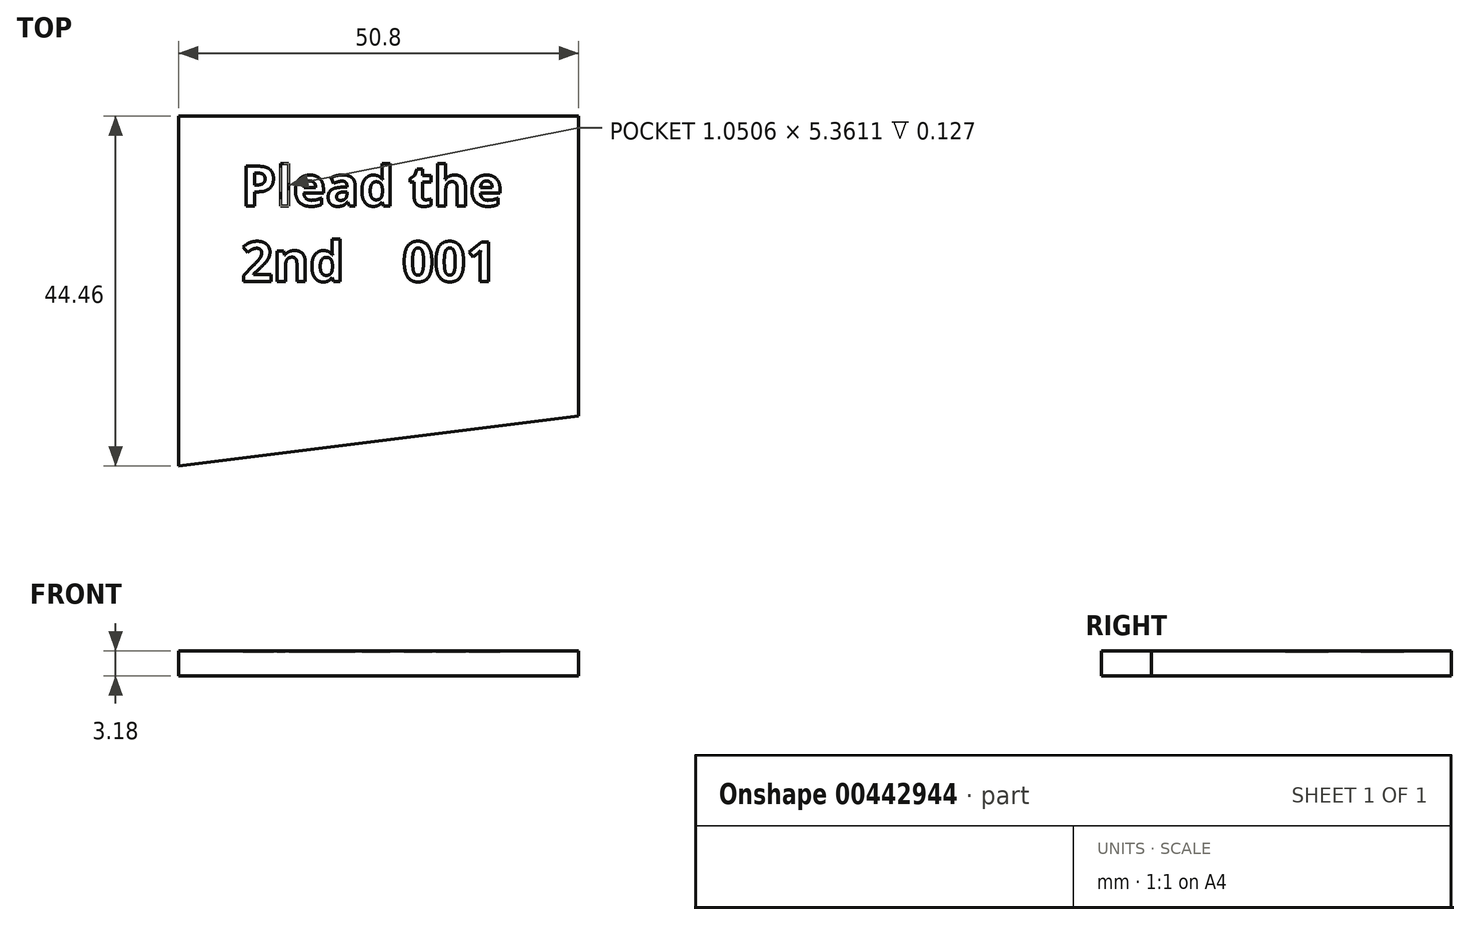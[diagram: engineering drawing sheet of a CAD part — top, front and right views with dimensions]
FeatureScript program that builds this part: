
annotation { "Feature Type Name" : "Feature", "Feature Type Description" : "" }
export const myFeature = defineFeature(function(context is Context, id is Id, definition is map)
    precondition{}
    {
        {
            var Q0;
            Q0=qCreatedBy(makeId("Top.planeOp"),FACE);
            var sketch = newSketch(context, id + "F0", { "sketchPlane" : qUnion([Q0])});
            skLineSegment(sketch, "E0.bottom", {"start": v(-57.15, -3.18) * mm, "end": v(-6.35, -3.18) * mm});
            skLineSegment(sketch, "E0.left", {"start": v(-57.15, -3.18) * mm, "end": v(-57.15, -47.63) * mm});
            skLineSegment(sketch, "E1", {"start": v(-6.35, -3.18) * mm, "end": v(-6.35, -41.28) * mm});
            skLineSegment(sketch, "E2", {"start": v(-57.15, -47.63) * mm, "end": v(-6.35, -41.28) * mm});
            skSolve(sketch);
        }
        {
            var Q0;
            Q0=makeQuery(id+"F0.imprint","IMPRINT",FACE,{"disambiguationData":[TD([[makeQuery(id+"F0.imprint","IMPRINT",EDGE,{"derivedFrom":sQuery(id+"F0.wireOp",EDGE,"E0.bottom")}),-1.0]])]});
            extrude(context, id + "F1", {"entities" : qUnion([Q0]), "depth" : 3.17 * mm});
        }
        {
            var Q0;
            Q0=makeQuery(id+"F1.opExtrude","CAP_FACE",FACE,{"disambiguationData":[OSD([sQuery(id+"F0.wireOp",EDGE,"E0.bottom"),sQuery(id+"F0.wireOp",EDGE,"E0.left"),sQuery(id+"F0.wireOp",EDGE,"E1"),sQuery(id+"F0.wireOp",EDGE,"E2")])],"isStart":false});
            var sketch = newSketch(context, id + "F2", { "sketchPlane" : qUnion([Q0])});
            skText(sketch, "E3", { "text": "Plead the 2nd", "fontName": "OpenSans-Italic.ttf"});
            const initialGuessF2  = {"E3": [-0.02232, 0.01193, 1, 0, 0.0052]};
            skSetInitialGuess(sketch, initialGuessF2);
            skSolve(sketch);
        }
        {
            var Q0;
            Q0=qSketchRegion(id+"F2",true);
            extrude(context, id + "F3", {"entities" : qUnion([Q0]), "operationType" : NewBodyOperationType.REMOVE, "oppositeDirection" : true, "depth" : 0.08 * mm});
        }
        {
            var Q0;
            Q0=makeQuery(id+"F1.opExtrude","CAP_FACE",FACE,{"disambiguationData":[OSD([sQuery(id+"F0.wireOp",EDGE,"E0.bottom"),sQuery(id+"F0.wireOp",EDGE,"E0.left"),sQuery(id+"F0.wireOp",EDGE,"E1"),sQuery(id+"F0.wireOp",EDGE,"E2")])],"isStart":false});
            var sketch = newSketch(context, id + "F4", { "sketchPlane" : qUnion([Q0])});
            skText(sketch, "E4", { "text": "Plead the\n2nd    001", "fontName": "OpenSans-Bold.ttf"});
            skLineSegment(sketch, "E5", {"start": v(-15.88, -25.17) * mm, "end": v(-54.6, -25.17) * mm, "construction": true});
            const initialGuessF4  = {"E4": [-0.04921, -0.0146, 1, 0, 0.00508]};
            skSetInitialGuess(sketch, initialGuessF4);
            skSolve(sketch);
        }
        {
            var Q0;
            Q0 = qSketchRegion(id + "F4", true);
            extrude(context, id + "F5", {"entities" : qUnion([Q0]), "operationType" : NewBodyOperationType.REMOVE, "oppositeDirection" : true, "depth" : 0.13 * mm});
        }
    });
